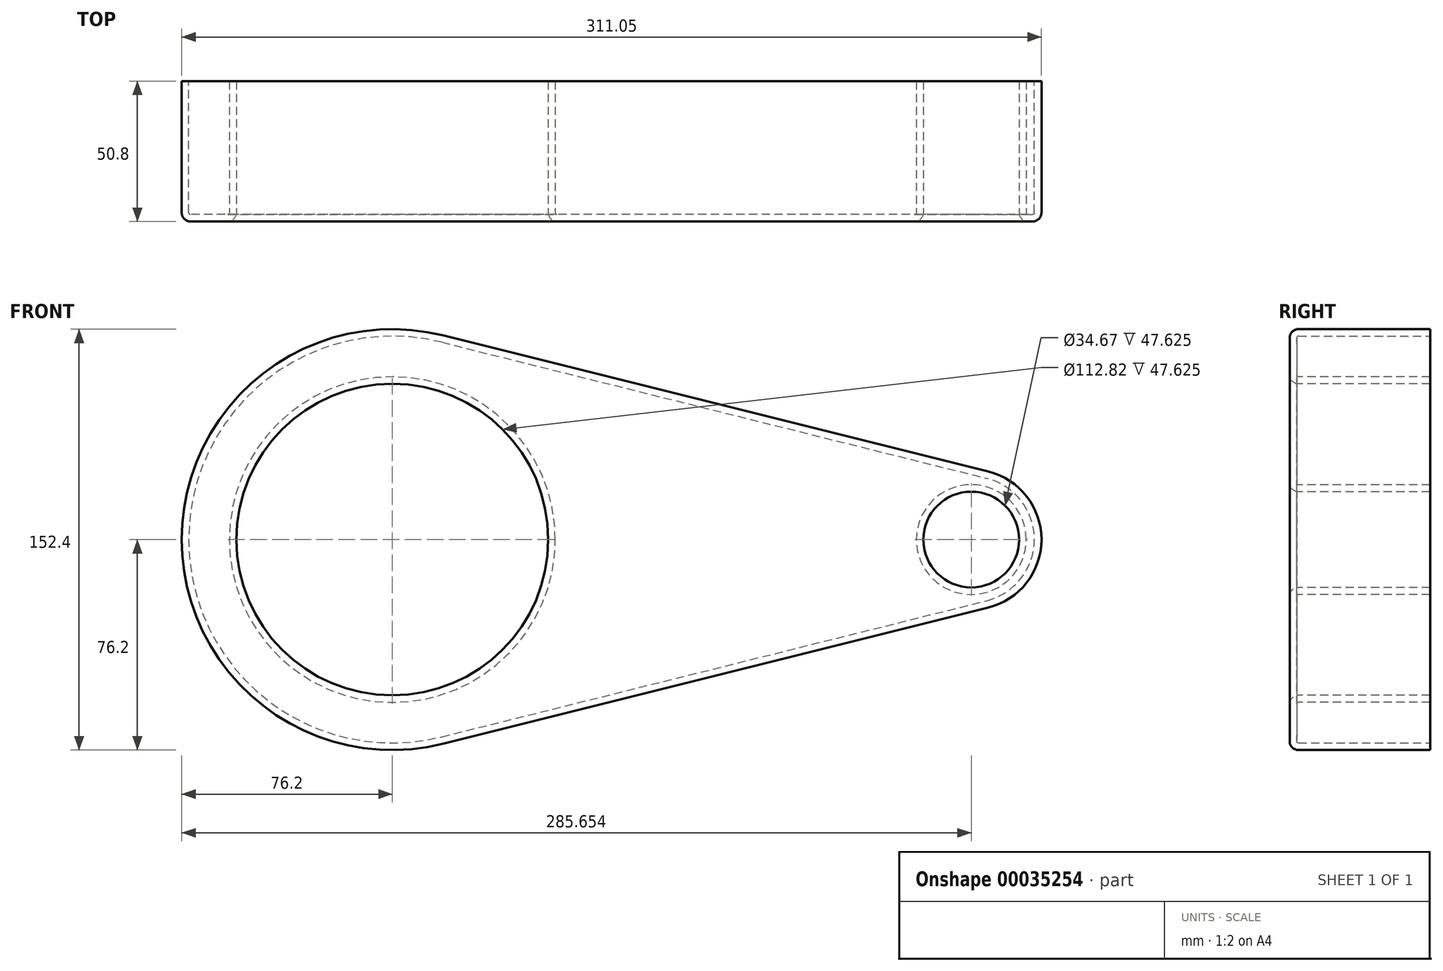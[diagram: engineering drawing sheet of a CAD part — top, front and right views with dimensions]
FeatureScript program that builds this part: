
annotation { "Feature Type Name" : "Feature", "Feature Type Description" : "" }
export const myFeature = defineFeature(function(context is Context, id is Id, definition is map)
    precondition{}
    {
        {
            var Q0;
            Q0=qCreatedBy(makeId("Front.planeOp"),FACE);
            var sketch = newSketch(context, id + "F0", { "sketchPlane" : qUnion([Q0])});
            skCircle(sketch, "E0", {"center": v(0, 0) * mm, "radius": 76.2 * mm});
            skCircle(sketch, "E1", {"center": v(209.45, 0) * mm, "radius": 25.4 * mm});
            skLineSegment(sketch, "E2", {"start": v(18.48, 73.92) * mm, "end": v(215.61, 24.64) * mm});
            skLineSegment(sketch, "E3", {"start": v(18.48, -73.92) * mm, "end": v(215.61, -24.64) * mm});
            skSolve(sketch);
        }
        {
            var Q0;
            {var subQ0=sQuery(id+"F0.wireOp",EDGE,"E2");Q0=makeQuery(id+"F0.imprint","IMPRINT",FACE,{"disambiguationData":[TD([[makeQuery(id+"F0.imprint","IMPRINT",EDGE,{"derivedFrom":subQ0}),-1.0]])]});}
            var Q1;
            {var subQ0=sQuery(id+"F0.wireOp",EDGE,"E1");var subQ1=makeQuery(id+"F0.imprint","INTERSECT",VERTEX,{"derivedFrom":[subQ0,sQuery(id+"F0.wireOp",EDGE,"E2")]});Q1=makeQuery(id+"F0.imprint","IMPRINT",FACE,{"disambiguationData":[TD([[makeQuery(id+"F0.imprint","IMPRINT",EDGE,{"disambiguationData":[TD([[subQ1,-1.0]])],"derivedFrom":subQ0}),1.0]])]});}
            var Q2;
            {var subQ0=sQuery(id+"F0.wireOp",EDGE,"E0");var subQ1=makeQuery(id+"F0.imprint","INTERSECT",VERTEX,{"derivedFrom":[subQ0,sQuery(id+"F0.wireOp",EDGE,"E2")]});Q2=makeQuery(id+"F0.imprint","IMPRINT",FACE,{"disambiguationData":[TD([[makeQuery(id+"F0.imprint","IMPRINT",EDGE,{"disambiguationData":[TD([[subQ1,-1.0]])],"derivedFrom":subQ0}),1.0]])]});}
            extrude(context, id + "F1", {"entities" : qUnion([Q0, Q1, Q2]), "depth" : 50.8 * mm});
        }
        {
            var Q0;
            Q0=makeQuery(id+"F1.opExtrude","CAP_FACE",FACE,{"disambiguationData":[OSD([sQuery(id+"F0.wireOp",EDGE,"E0"),sQuery(id+"F0.wireOp",EDGE,"E1"),sQuery(id+"F0.wireOp",EDGE,"E2"),sQuery(id+"F0.wireOp",EDGE,"E3")])],"isStart":false});
            var sketch = newSketch(context, id + "F2", { "sketchPlane" : qUnion([Q0])});
            skCircle(sketch, "E4", {"center": v(0, 0) * mm, "radius": 56.41 * mm});
            skCircle(sketch, "E5", {"center": v(209.45, 0) * mm, "radius": 17.33 * mm});
            skSolve(sketch);
        }
        {
            var Q0;
            Q0=makeQuery(id+"F2.imprint","IMPRINT",FACE,{"disambiguationData":[TD([[makeQuery(id+"F2.imprint","IMPRINT",EDGE,{"derivedFrom":sQuery(id+"F2.wireOp",EDGE,"E4")}),1.0]])]});
            var Q1;
            Q1=makeQuery(id+"F2.imprint","IMPRINT",FACE,{"disambiguationData":[TD([[makeQuery(id+"F2.imprint","IMPRINT",EDGE,{"derivedFrom":sQuery(id+"F2.wireOp",EDGE,"E5")}),1.0]])]});
            extrude(context, id + "F3", {"entities" : qUnion([Q0, Q1]), "operationType" : NewBodyOperationType.REMOVE, "oppositeDirection" : true, "depth" : 50.8 * mm});
        }
        {
            var Q0;
            Q0=makeQuery(id+"F1.opExtrude","CAP_FACE",FACE,{"disambiguationData":[OSD([sQuery(id+"F0.wireOp",EDGE,"E0"),sQuery(id+"F0.wireOp",EDGE,"E1"),sQuery(id+"F0.wireOp",EDGE,"E2"),sQuery(id+"F0.wireOp",EDGE,"E3")])],"isStart":false});
            var Q1;
            Q1=makeQuery(id+"F3.boolean.opBoolean","COPY",FACE,{"derivedFrom":makeQuery(id+"F3.opExtrude","CAP_FACE",FACE,{"disambiguationData":[OSD([sQuery(id+"F2.wireOp",EDGE,"E4")])],"isStart":false})});
            var Q2;
            Q2=makeQuery(id+"F3.boolean.opBoolean","COPY",FACE,{"derivedFrom":makeQuery(id+"F3.opExtrude","CAP_FACE",FACE,{"disambiguationData":[OSD([sQuery(id+"F2.wireOp",EDGE,"E5")])],"isStart":false})});
            fillet(context, id + "F4", {"entities" : qUnion([Q0, Q1, Q2]), "radius" : 3.17 * mm, "tangentPropagation" : true, "allowEdgeOverflow" : false});
        }
        {
            var Q0;
            Q0=makeQuery(id+"F1.opExtrude","CAP_FACE",FACE,{"disambiguationData":[OSD([sQuery(id+"F0.wireOp",EDGE,"E0"),sQuery(id+"F0.wireOp",EDGE,"E1"),sQuery(id+"F0.wireOp",EDGE,"E2"),sQuery(id+"F0.wireOp",EDGE,"E3")])],"isStart":true});
            shell(context, id + "F5", {"entities" : qUnion([Q0]), "thickness" : 2.54 * mm});
        }
    });
